# Revit family: Basic PDU with local power meter
name_source: partatom
category: Installations électriques
units: mm (PartAtom-declared; Revit-internal decimal feet)

## family parameters
Basée sur le plan de construction = Non
Conserver l'orientation des annotations = Non
Cote de connecteur circulaire = Utiliser le diamètre
Couper avec des vides une fois chargée = Non
Numéro OmniClass = 23.80.00.00
Partagée = Non
Point de calcul de pièce = Non
Titre OmniClass = Electric Power and Lighting
Toujours verticalement = Oui
Type d'élément = Normal

## types (2) — shared parameters
Application class = EC002762
BIM wording = Linkeo DATA CENTER BASIC PDU
Color = Black
Connectable by internet box = Non
E-catalogue link = https://www.legrand.fr
Fabricant = LEGRAND
Function = Unit DE DISTRIBUTION D'ENERGIE
IP = IP20
Mounting direction = Vertical
Power frequency = 50-50
Prise_alimentation = Alimentation : Prise rotative
Programming way = Non applicable
RAL Number = 9017
Terminal marking indication = Oui
type of voltage = AC
zero-valued in all types: Elévation par défaut

## per-type parameters (varying)
| type | 646166 | 646170 | Cable cross section MIN_MAX | Depth (mm) | Description | GTIN | Legrand part number | Length | Number of C13 outlets | Number of C19 outlets | Number of MCB | Number of phases | Profondeur cuve + capot | Standby consumption | Supply current | Type of electric connection | Width (mm) |
| PDU 0U LPM 1P 32A 20xC13+4xC19 | Oui | Non | 6-6 | 85 mm | PDU BASIC 0U LPM 1 PHASE 32A , 20+4 C13/C19 LOCKING OUTLETS , IEC 60309 | 3414972471435 | LG-646966 | 1227 mm | 20 | 4 | 2 | 1 | 58 mm | 37 mA | 32-32 | CEE 32 A | 44 mm |
| PDU HD 0U LPM 3P 16A 36xC13+6xC19 | Non | Oui | 2.5-2.5 | 92 mm | PDU HD BASIC 0U LPM 3 PHASE 16A , 36+6 C13/C19  LOCKING OUTLETS , IEC 60309 | 3414972471442 | LG-646970 | 1248 mm  [stored 4.09449 ft] | 36 | 6 | 0 | 3 | 65 mm  [stored 0.213255 ft] | 71 mA | 16-16 | CEE 16 A | 52 mm  [stored 0.170604 ft] |

note: [stored X ft] marks values corroborated as IEEE doubles in the binary element streams (Revit-internal decimal feet)
